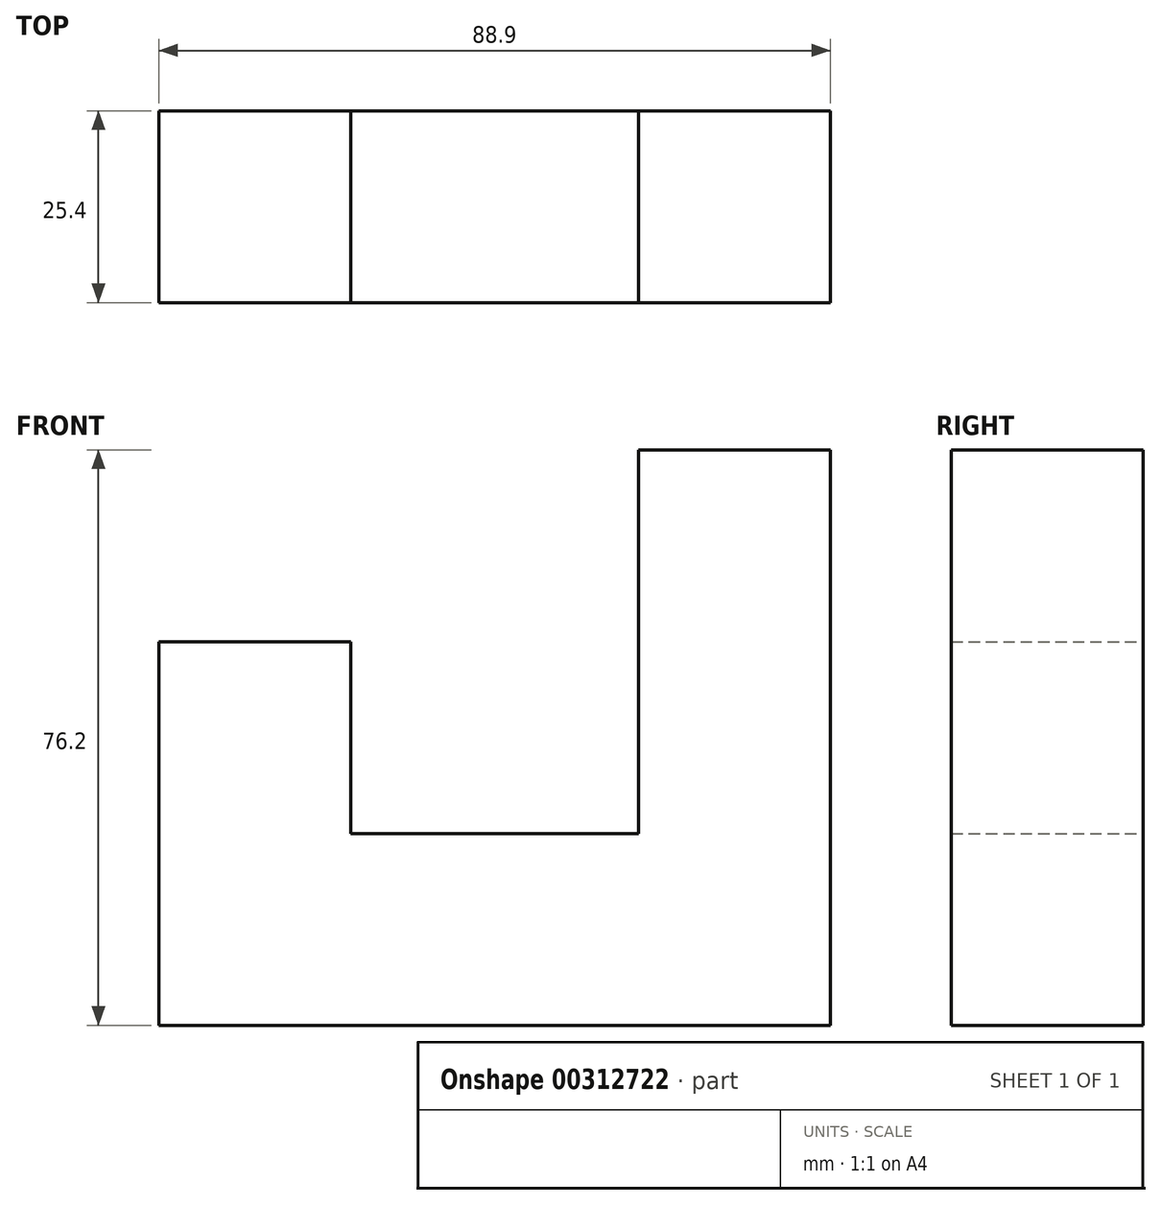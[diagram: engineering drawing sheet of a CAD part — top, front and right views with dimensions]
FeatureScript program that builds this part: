
annotation { "Feature Type Name" : "Feature", "Feature Type Description" : "" }
export const myFeature = defineFeature(function(context is Context, id is Id, definition is map)
    precondition{}
    {
        {
            var Q0;
            Q0=qCreatedBy(makeId("Front.planeOp"),FACE);
            var sketch = newSketch(context, id + "F0", { "sketchPlane" : qUnion([Q0])});
            skLineSegment(sketch, "E0", {"start": v(-42.36, -32.65) * mm, "end": v(46.54, -32.65) * mm});
            skLineSegment(sketch, "E1", {"start": v(46.54, -32.65) * mm, "end": v(46.54, 43.55) * mm});
            skLineSegment(sketch, "E2", {"start": v(46.54, 43.55) * mm, "end": v(21.14, 43.55) * mm});
            skLineSegment(sketch, "E3", {"start": v(21.14, 43.55) * mm, "end": v(21.14, -7.25) * mm});
            skLineSegment(sketch, "E4", {"start": v(21.14, -7.25) * mm, "end": v(-16.96, -7.25) * mm});
            skLineSegment(sketch, "E5", {"start": v(-16.96, -7.25) * mm, "end": v(-16.96, 18.15) * mm});
            skLineSegment(sketch, "E6", {"start": v(-16.96, 18.15) * mm, "end": v(-42.36, 18.15) * mm});
            skLineSegment(sketch, "E7", {"start": v(-42.36, -32.65) * mm, "end": v(-42.36, 18.15) * mm});
            skSolve(sketch);
        }
        {
            var Q0;
            Q0=makeQuery(id+"F0.imprint","IMPRINT",FACE,{"disambiguationData":[TD([[makeQuery(id+"F0.imprint","IMPRINT",EDGE,{"derivedFrom":sQuery(id+"F0.wireOp",EDGE,"aguI3ylT-zIaB-Fvg1-q9KX-QLK8P4eupsc8")}),1.0]])]});
            var Q1;
            Q1=makeQuery(id+"F0.imprint","IMPRINT",FACE,{"disambiguationData":[TD([[makeQuery(id+"F0.imprint","IMPRINT",EDGE,{"derivedFrom":sQuery(id+"F0.wireOp",EDGE,"E0")}),1.0]])]});
            extrude(context, id + "F1", {"entities" : qUnion([Q0, Q1]), "depth" : 25.4 * mm});
        }
    });
